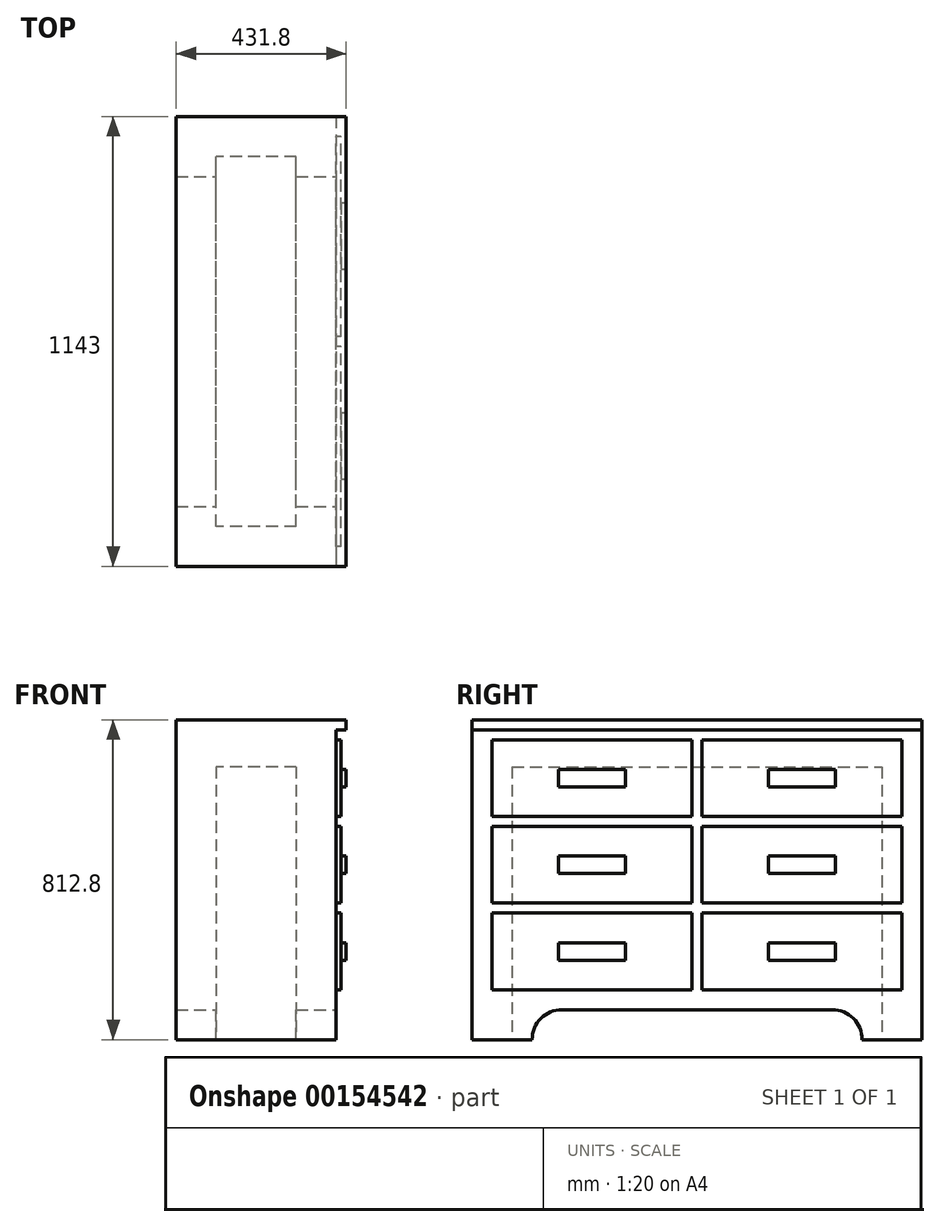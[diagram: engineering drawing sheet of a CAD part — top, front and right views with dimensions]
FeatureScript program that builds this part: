
annotation { "Feature Type Name" : "Feature", "Feature Type Description" : "" }
export const myFeature = defineFeature(function(context is Context, id is Id, definition is map)
    precondition{}
    {
        {
            var Q0;
            Q0=qCreatedBy(makeId("Top.planeOp"),FACE);
            var sketch = newSketch(context, id + "F0", { "sketchPlane" : qUnion([Q0])});
            skLineSegment(sketch, "E0.bottom", {"start": v(-203.2, 571.5) * mm, "end": v(203.2, 571.5) * mm});
            skLineSegment(sketch, "E0.top", {"start": v(-203.2, -571.5) * mm, "end": v(203.2, -571.5) * mm});
            skLineSegment(sketch, "E0.left", {"start": v(-203.2, 571.5) * mm, "end": v(-203.2, -571.5) * mm});
            skLineSegment(sketch, "E0.right", {"start": v(203.2, 571.5) * mm, "end": v(203.2, -571.5) * mm});
            skPoint(sketch, "E0.middle", {"position": v(0, 0) * mm});
            skSolve(sketch);
        }
        {
            var Q0;
            Q0=makeQuery(id+"F0.imprint","IMPRINT",FACE,{"disambiguationData":[TD([[makeQuery(id+"F0.imprint","IMPRINT",EDGE,{"derivedFrom":sQuery(id+"F0.wireOp",EDGE,"E0.bottom")}),-1.0]])]});
            extrude(context, id + "F1", {"entities" : qUnion([Q0]), "depth" : 812.8 * mm});
        }
        {
            var Q0;
            Q0=makeQuery(id+"F1.opExtrude","CAP_FACE",FACE,{"disambiguationData":[OSD([sQuery(id+"F0.wireOp",EDGE,"E0.bottom"),sQuery(id+"F0.wireOp",EDGE,"E0.top"),sQuery(id+"F0.wireOp",EDGE,"E0.left"),sQuery(id+"F0.wireOp",EDGE,"E0.right")])],"isStart":false});
            var sketch = newSketch(context, id + "F2", { "sketchPlane" : qUnion([Q0])});
            skLineSegment(sketch, "E1.bottom", {"start": v(-203.2, 571.5) * mm, "end": v(228.6, 571.5) * mm});
            skLineSegment(sketch, "E1.top", {"start": v(-203.2, -571.5) * mm, "end": v(228.6, -571.5) * mm});
            skLineSegment(sketch, "E1.left", {"start": v(-203.2, 571.5) * mm, "end": v(-203.2, -571.5) * mm});
            skLineSegment(sketch, "E1.right", {"start": v(228.6, 571.5) * mm, "end": v(228.6, -571.5) * mm});
            skSolve(sketch);
        }
        {
            var Q0;
            {var subQ2=sQuery(id+"F2.wireOp",EDGE,"E1.right");Q0=makeQuery(id+"F2.imprint","IMPRINT",FACE,{"disambiguationData":[TD([[makeQuery(id+"F2.imprint","IMPRINT",EDGE,{"derivedFrom":subQ2}),-1.0]])]});}
            extrude(context, id + "F3", {"entities" : qUnion([Q0]), "operationType" : NewBodyOperationType.ADD, "oppositeDirection" : true, "depth" : 25.4 * mm});
        }
        {
            var Q0;
            Q0=makeQuery(id+"F1.opExtrude","SWEPT_FACE",FACE,{"disambiguationData":[OSD([sQuery(id+"F0.wireOp",EDGE,"E0.right")])]});
            var sketch = newSketch(context, id + "F4", { "sketchPlane" : qUnion([Q0])});
            skLineSegment(sketch, "E2.bottom", {"start": v(-520.7, 762) * mm, "end": v(-12.7, 762) * mm});
            skLineSegment(sketch, "E2.top", {"start": v(-520.7, 567.27) * mm, "end": v(-12.7, 567.27) * mm});
            skLineSegment(sketch, "E2.left", {"start": v(-520.7, 762) * mm, "end": v(-520.7, 567.27) * mm});
            skLineSegment(sketch, "E2.right", {"start": v(-12.7, 762) * mm, "end": v(-12.7, 567.27) * mm});
            skLineSegment(sketch, "E3.bottom", {"start": v(12.7, 762) * mm, "end": v(520.7, 762) * mm});
            skLineSegment(sketch, "E3.top", {"start": v(12.7, 567.27) * mm, "end": v(520.7, 567.27) * mm});
            skLineSegment(sketch, "E3.left", {"start": v(12.7, 762) * mm, "end": v(12.7, 567.27) * mm});
            skLineSegment(sketch, "E3.right", {"start": v(520.7, 762) * mm, "end": v(520.7, 567.27) * mm});
            skLineSegment(sketch, "E4.bottom", {"start": v(520.7, 541.87) * mm, "end": v(12.7, 541.87) * mm});
            skLineSegment(sketch, "E4.top", {"start": v(520.7, 347.13) * mm, "end": v(12.7, 347.13) * mm});
            skLineSegment(sketch, "E4.left", {"start": v(520.7, 541.87) * mm, "end": v(520.7, 347.13) * mm});
            skLineSegment(sketch, "E4.right", {"start": v(12.7, 541.87) * mm, "end": v(12.7, 347.13) * mm});
            skLineSegment(sketch, "E5.bottom", {"start": v(-12.7, 347.13) * mm, "end": v(-520.7, 347.13) * mm});
            skLineSegment(sketch, "E5.top", {"start": v(-12.7, 541.87) * mm, "end": v(-520.7, 541.87) * mm});
            skLineSegment(sketch, "E5.left", {"start": v(-12.7, 347.13) * mm, "end": v(-12.7, 541.87) * mm});
            skLineSegment(sketch, "E5.right", {"start": v(-520.7, 347.13) * mm, "end": v(-520.7, 541.87) * mm});
            skLineSegment(sketch, "E6.bottom", {"start": v(-520.7, 321.73) * mm, "end": v(-12.7, 321.73) * mm});
            skLineSegment(sketch, "E6.top", {"start": v(-520.7, 127) * mm, "end": v(-12.7, 127) * mm});
            skLineSegment(sketch, "E6.left", {"start": v(-520.7, 321.73) * mm, "end": v(-520.7, 127) * mm});
            skLineSegment(sketch, "E6.right", {"start": v(-12.7, 321.73) * mm, "end": v(-12.7, 127) * mm});
            skLineSegment(sketch, "E7.bottom", {"start": v(12.7, 321.73) * mm, "end": v(520.7, 321.73) * mm});
            skLineSegment(sketch, "E7.top", {"start": v(12.7, 127) * mm, "end": v(520.7, 127) * mm});
            skLineSegment(sketch, "E7.left", {"start": v(12.7, 321.73) * mm, "end": v(12.7, 127) * mm});
            skLineSegment(sketch, "E7.right", {"start": v(520.7, 321.73) * mm, "end": v(520.7, 127) * mm});
            skLineSegment(sketch, "E8", {"start": v(-419.1, 0) * mm, "end": v(-419.1, 0) * mm});
            skLineSegment(sketch, "E9", {"start": v(-342.9, 76.2) * mm, "end": v(342.9, 76.2) * mm});
            skLineSegment(sketch, "E10", {"start": v(419.1, 0) * mm, "end": v(419.1, 0) * mm});
            skPoint(sketch, "E11.visualSharp", {"position": v(-419.1, 76.2) * mm});
            skArc(sketch, "E11.filletArc", {"start": v(-342.9, 76.2) * mm, "mid": v(-396.78, 53.88) * mm, "end": v(-419.1, 0) * mm});
            skPoint(sketch, "E12.visualSharp", {"position": v(419.1, 76.2) * mm});
            skArc(sketch, "E12.filletArc", {"start": v(419.1, 0) * mm, "mid": v(396.78, 53.88) * mm, "end": v(342.9, 76.2) * mm});
            skLineSegment(sketch, "E13", {"start": v(-419.1, 0) * mm, "end": v(419.1, 0) * mm});
            skSolve(sketch);
        }
        {
            var Q0;
            Q0=makeQuery(id+"F4.imprint","IMPRINT",FACE,{"disambiguationData":[TD([[makeQuery(id+"F4.imprint","IMPRINT",EDGE,{"derivedFrom":sQuery(id+"F4.wireOp",EDGE,"E2.bottom")}),-1.0]])]});
            var Q1;
            Q1=makeQuery(id+"F4.imprint","IMPRINT",FACE,{"disambiguationData":[TD([[makeQuery(id+"F4.imprint","IMPRINT",EDGE,{"derivedFrom":sQuery(id+"F4.wireOp",EDGE,"E3.bottom")}),-1.0]])]});
            var Q2;
            Q2=makeQuery(id+"F4.imprint","IMPRINT",FACE,{"disambiguationData":[TD([[makeQuery(id+"F4.imprint","IMPRINT",EDGE,{"derivedFrom":sQuery(id+"F4.wireOp",EDGE,"E4.bottom")}),1.0]])]});
            var Q3;
            Q3=makeQuery(id+"F4.imprint","IMPRINT",FACE,{"disambiguationData":[TD([[makeQuery(id+"F4.imprint","IMPRINT",EDGE,{"derivedFrom":sQuery(id+"F4.wireOp",EDGE,"E5.bottom")}),-1.0]])]});
            var Q4;
            Q4=makeQuery(id+"F4.imprint","IMPRINT",FACE,{"disambiguationData":[TD([[makeQuery(id+"F4.imprint","IMPRINT",EDGE,{"derivedFrom":sQuery(id+"F4.wireOp",EDGE,"E6.bottom")}),-1.0]])]});
            var Q5;
            Q5=makeQuery(id+"F4.imprint","IMPRINT",FACE,{"disambiguationData":[TD([[makeQuery(id+"F4.imprint","IMPRINT",EDGE,{"derivedFrom":sQuery(id+"F4.wireOp",EDGE,"E7.bottom")}),-1.0]])]});
            extrude(context, id + "F5", {"entities" : qUnion([Q0, Q1, Q2, Q3, Q4, Q5]), "operationType" : NewBodyOperationType.ADD, "depth" : 12.7 * mm});
        }
        {
            var Q0;
            Q0=makeQuery(id+"F4.imprint","IMPRINT",FACE,{"disambiguationData":[TD([[makeQuery(id+"F4.imprint","IMPRINT",EDGE,{"derivedFrom":sQuery(id+"F4.wireOp",EDGE,"E9")}),-1.0]])]});
            extrude(context, id + "F6", {"entities" : qUnion([Q0]), "operationType" : NewBodyOperationType.REMOVE, "endBound" : BoundingType.THROUGH_ALL, "oppositeDirection" : true, "depth" : 30.48 * mm});
        }
        {
            var Q0;
            Q0=makeQuery(id+"F5.opExtrude","CAP_FACE",FACE,{"disambiguationData":[OSD([sQuery(id+"F4.wireOp",EDGE,"E2.bottom"),sQuery(id+"F4.wireOp",EDGE,"E2.top"),sQuery(id+"F4.wireOp",EDGE,"E2.left"),sQuery(id+"F4.wireOp",EDGE,"E2.right")])],"isStart":false});
            var sketch = newSketch(context, id + "F7", { "sketchPlane" : qUnion([Q0])});
            skLineSegment(sketch, "E14", {"start": v(-266.7, 762) * mm, "end": v(-266.7, 567.27) * mm, "construction": true});
            skLineSegment(sketch, "E15.bottom", {"start": v(-181.65, 686.71) * mm, "end": v(-351.75, 686.71) * mm});
            skLineSegment(sketch, "E15.top", {"start": v(-181.65, 642.55) * mm, "end": v(-351.75, 642.55) * mm});
            skLineSegment(sketch, "E15.left", {"start": v(-181.65, 686.71) * mm, "end": v(-181.65, 642.55) * mm});
            skLineSegment(sketch, "E15.right", {"start": v(-351.75, 686.71) * mm, "end": v(-351.75, 642.55) * mm});
            skPoint(sketch, "E15.middle", {"position": v(-266.7, 664.63) * mm});
            skLineSegment(sketch, "E16.0.1.0", {"start": v(-181.65, 466.34) * mm, "end": v(-351.75, 466.34) * mm});
            skLineSegment(sketch, "E16.0.1.1", {"start": v(-181.65, 466.34) * mm, "end": v(-181.65, 422.18) * mm});
            skLineSegment(sketch, "E16.0.1.2", {"start": v(-181.65, 422.18) * mm, "end": v(-351.75, 422.18) * mm});
            skLineSegment(sketch, "E16.0.1.3", {"start": v(-351.75, 466.34) * mm, "end": v(-351.75, 422.18) * mm});
            skLineSegment(sketch, "E16.0.2.0", {"start": v(-181.65, 245.97) * mm, "end": v(-351.75, 245.97) * mm});
            skLineSegment(sketch, "E16.0.2.1", {"start": v(-181.65, 245.97) * mm, "end": v(-181.65, 201.81) * mm});
            skLineSegment(sketch, "E16.0.2.2", {"start": v(-181.65, 201.81) * mm, "end": v(-351.75, 201.81) * mm});
            skLineSegment(sketch, "E16.0.2.3", {"start": v(-351.75, 245.97) * mm, "end": v(-351.75, 201.81) * mm});
            skLineSegment(sketch, "E16.1.0.0", {"start": v(351.75, 686.71) * mm, "end": v(181.65, 686.71) * mm});
            skLineSegment(sketch, "E16.1.0.1", {"start": v(351.75, 686.71) * mm, "end": v(351.75, 642.55) * mm});
            skLineSegment(sketch, "E16.1.0.2", {"start": v(351.75, 642.55) * mm, "end": v(181.65, 642.55) * mm});
            skLineSegment(sketch, "E16.1.0.3", {"start": v(181.65, 686.71) * mm, "end": v(181.65, 642.55) * mm});
            skLineSegment(sketch, "E16.1.1.0", {"start": v(351.75, 466.34) * mm, "end": v(181.65, 466.34) * mm});
            skLineSegment(sketch, "E16.1.1.1", {"start": v(351.75, 466.34) * mm, "end": v(351.75, 422.18) * mm});
            skLineSegment(sketch, "E16.1.1.2", {"start": v(351.75, 422.18) * mm, "end": v(181.65, 422.18) * mm});
            skLineSegment(sketch, "E16.1.1.3", {"start": v(181.65, 466.34) * mm, "end": v(181.65, 422.18) * mm});
            skLineSegment(sketch, "E16.1.2.0", {"start": v(351.75, 245.97) * mm, "end": v(181.65, 245.97) * mm});
            skLineSegment(sketch, "E16.1.2.1", {"start": v(351.75, 245.97) * mm, "end": v(351.75, 201.81) * mm});
            skLineSegment(sketch, "E16.1.2.2", {"start": v(351.75, 201.81) * mm, "end": v(181.65, 201.81) * mm});
            skLineSegment(sketch, "E16.1.2.3", {"start": v(181.65, 245.97) * mm, "end": v(181.65, 201.81) * mm});
            skLineSegment(sketch, "E16.direction1", {"start": v(-351.75, 642.55) * mm, "end": v(181.65, 642.55) * mm, "construction": true});
            skLineSegment(sketch, "E16.direction2", {"start": v(-351.75, 642.55) * mm, "end": v(-351.75, 422.18) * mm, "construction": true});
            skSolve(sketch);
        }
        {
            var Q0;
            Q0=makeQuery(id+"F7.imprint","IMPRINT",FACE,{"disambiguationData":[TD([[makeQuery(id+"F7.imprint","IMPRINT",EDGE,{"derivedFrom":sQuery(id+"F7.wireOp",EDGE,"E15.bottom")}),1.0]])]});
            var Q1;
            Q1=makeQuery(id+"F7.imprint","IMPRINT",FACE,{"disambiguationData":[TD([[makeQuery(id+"F7.imprint","IMPRINT",EDGE,{"derivedFrom":sQuery(id+"F7.wireOp",EDGE,"E16.1.0.0")}),1.0]])]});
            var Q2;
            Q2=makeQuery(id+"F7.imprint","IMPRINT",FACE,{"disambiguationData":[TD([[makeQuery(id+"F7.imprint","IMPRINT",EDGE,{"derivedFrom":sQuery(id+"F7.wireOp",EDGE,"E16.1.1.0")}),1.0]])]});
            var Q3;
            Q3=makeQuery(id+"F7.imprint","IMPRINT",FACE,{"disambiguationData":[TD([[makeQuery(id+"F7.imprint","IMPRINT",EDGE,{"derivedFrom":sQuery(id+"F7.wireOp",EDGE,"E16.1.2.0")}),1.0]])]});
            var Q4;
            Q4=makeQuery(id+"F7.imprint","IMPRINT",FACE,{"disambiguationData":[TD([[makeQuery(id+"F7.imprint","IMPRINT",EDGE,{"derivedFrom":sQuery(id+"F7.wireOp",EDGE,"E16.0.2.0")}),1.0]])]});
            var Q5;
            Q5=makeQuery(id+"F7.imprint","IMPRINT",FACE,{"disambiguationData":[TD([[makeQuery(id+"F7.imprint","IMPRINT",EDGE,{"derivedFrom":sQuery(id+"F7.wireOp",EDGE,"E16.0.1.0")}),1.0]])]});
            extrude(context, id + "F8", {"entities" : qUnion([Q0, Q1, Q2, Q3, Q4, Q5]), "operationType" : NewBodyOperationType.ADD, "depth" : 12.7 * mm});
        }
        {
            var Q0;
            {var subQ0=sQuery(id+"F0.wireOp",EDGE,"E0.right");var subQ1=sQuery(id+"F0.wireOp",EDGE,"E0.left");var subQ2=sQuery(id+"F0.wireOp",EDGE,"E0.top");Q0=makeQuery(id+"F6.boolean.opBoolean","SPLIT",FACE,{"disambiguationData":[TD([makeQuery(id+"F1.opExtrude","SWEPT_FACE",FACE,{"disambiguationData":[OSD([subQ2])]})])],"derivedFrom":makeQuery(id+"F1.opExtrude","CAP_FACE",FACE,{"disambiguationData":[OSD([sQuery(id+"F0.wireOp",EDGE,"E0.bottom"),subQ2,subQ1,subQ0])],"isStart":true})});}
            var sketch = newSketch(context, id + "F9", { "sketchPlane" : qUnion([Q0])});
            skLineSegment(sketch, "E17.bottom", {"start": v(101.6, 469.9) * mm, "end": v(-101.6, 469.9) * mm});
            skLineSegment(sketch, "E17.top", {"start": v(101.6, -469.9) * mm, "end": v(-101.6, -469.9) * mm});
            skLineSegment(sketch, "E17.left", {"start": v(101.6, 469.9) * mm, "end": v(101.6, -469.9) * mm});
            skLineSegment(sketch, "E17.right", {"start": v(-101.6, 469.9) * mm, "end": v(-101.6, -469.9) * mm});
            skSolve(sketch);
        }
        {
            var Q0;
            {var subQ0=sQuery(id+"F9.wireOp",EDGE,"E17.top");Q0=makeQuery(id+"F9.imprint","IMPRINT",FACE,{"disambiguationData":[TD([[makeQuery(id+"F9.imprint","IMPRINT",EDGE,{"derivedFrom":subQ0}),-1.0]])]});}
            var Q1;
            {var subQ0=sQuery(id+"F9.wireOp",EDGE,"E17.bottom");Q1=makeQuery(id+"F9.imprint","IMPRINT",FACE,{"disambiguationData":[TD([[makeQuery(id+"F9.imprint","IMPRINT",EDGE,{"derivedFrom":subQ0}),1.0]])]});}
            extrude(context, id + "F10", {"entities" : qUnion([Q0, Q1]), "operationType" : NewBodyOperationType.REMOVE, "oppositeDirection" : true, "depth" : 693.42 * mm});
        }
    });
